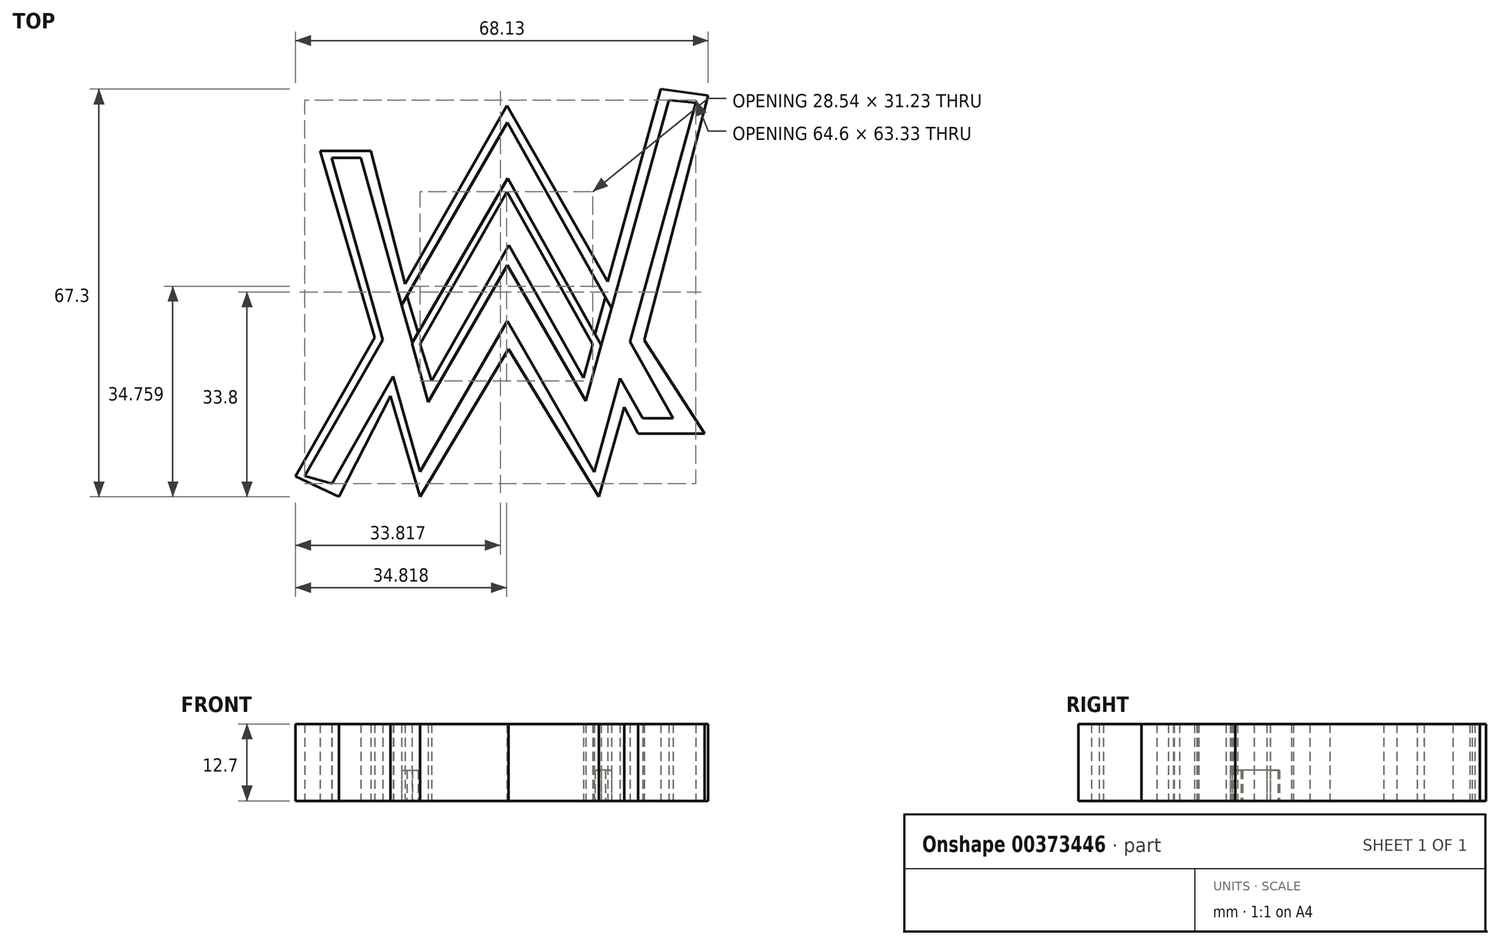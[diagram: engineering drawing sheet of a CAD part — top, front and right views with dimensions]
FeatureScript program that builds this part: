
annotation { "Feature Type Name" : "Feature", "Feature Type Description" : "" }
export const myFeature = defineFeature(function(context is Context, id is Id, definition is map)
    precondition{}
    {
        {
            var Q0;
            Q0=qCreatedBy(makeId("Top.planeOp"),FACE);
            var sketch = newSketch(context, id + "F0", { "sketchPlane" : qUnion([Q0])});
            skLineSegment(sketch, "E0", {"start": v(-32.07, -30.83) * mm, "end": v(-19.22, -8.32) * mm});
            skLineSegment(sketch, "E1", {"start": v(-19.22, -8.32) * mm, "end": v(-27.67, 21.68) * mm});
            skLineSegment(sketch, "E2", {"start": v(-27.67, 21.68) * mm, "end": v(-22.79, 21.68) * mm});
            skLineSegment(sketch, "E3", {"start": v(-22.79, 21.68) * mm, "end": v(-16.07, -2.6) * mm});
            skLineSegment(sketch, "E4", {"start": v(-16.07, -2.6) * mm, "end": v(1.36, 27.56) * mm});
            skLineSegment(sketch, "E5", {"start": v(1.36, 27.56) * mm, "end": v(18.6, -3.14) * mm});
            skLineSegment(sketch, "E6", {"start": v(18.6, -3.14) * mm, "end": v(28.06, 31.21) * mm});
            skLineSegment(sketch, "E7", {"start": v(28.06, 31.21) * mm, "end": v(32.52, 30.76) * mm});
            skLineSegment(sketch, "E8", {"start": v(32.52, 30.76) * mm, "end": v(21.67, -8.63) * mm});
            skLineSegment(sketch, "E9", {"start": v(21.67, -8.63) * mm, "end": v(28.75, -21.3) * mm});
            skLineSegment(sketch, "E10", {"start": v(28.75, -21.3) * mm, "end": v(23.7, -21.3) * mm});
            skLineSegment(sketch, "E11", {"start": v(23.7, -21.3) * mm, "end": v(20, -14.7) * mm});
            skLineSegment(sketch, "E12", {"start": v(20, -14.7) * mm, "end": v(15.7, -30.17) * mm});
            skLineSegment(sketch, "E13", {"start": v(15.7, -30.17) * mm, "end": v(1.36, -5.25) * mm});
            skLineSegment(sketch, "E14", {"start": v(1.36, -5.25) * mm, "end": v(-13.04, -30.13) * mm});
            skLineSegment(sketch, "E15", {"start": v(-13.04, -30.13) * mm, "end": v(-17.44, -14.62) * mm});
            skLineSegment(sketch, "E16", {"start": v(-17.44, -14.62) * mm, "end": v(-17.5, -14.4) * mm});
            skLineSegment(sketch, "E17", {"start": v(-17.5, -14.4) * mm, "end": v(-27.56, -32.11) * mm});
            skLineSegment(sketch, "E18", {"start": v(-27.56, -32.11) * mm, "end": v(-32.07, -30.83) * mm});
            skLineSegment(sketch, "E19", {"start": v(1.43, 18.3) * mm, "end": v(16.89, -9.22) * mm});
            skLineSegment(sketch, "E20", {"start": v(16.89, -9.22) * mm, "end": v(14.34, -18.46) * mm});
            skLineSegment(sketch, "E21", {"start": v(14.34, -18.46) * mm, "end": v(1.37, 3.98) * mm});
            skLineSegment(sketch, "E22", {"start": v(1.37, 3.98) * mm, "end": v(-11.69, -18.6) * mm});
            skLineSegment(sketch, "E23", {"start": v(-11.69, -18.6) * mm, "end": v(-14.35, -8.89) * mm});
            skLineSegment(sketch, "E24", {"start": v(-14.35, -8.89) * mm, "end": v(1.43, 18.3) * mm});
            skLineSegment(sketch, "E25", {"start": v(-33.59, -30.85) * mm, "end": v(-20.52, -7.97) * mm});
            skLineSegment(sketch, "E26", {"start": v(-20.52, -7.97) * mm, "end": v(-29.53, 22.83) * mm});
            skLineSegment(sketch, "E27", {"start": v(-29.53, 22.83) * mm, "end": v(-21.16, 22.83) * mm});
            skLineSegment(sketch, "E28", {"start": v(-21.16, 22.83) * mm, "end": v(-15.52, 0.88) * mm});
            skLineSegment(sketch, "E29", {"start": v(-15.52, 0.88) * mm, "end": v(1.31, 30.35) * mm});
            skLineSegment(sketch, "E30", {"start": v(1.31, 30.35) * mm, "end": v(17.97, 1.23) * mm});
            skLineSegment(sketch, "E31", {"start": v(17.97, 1.23) * mm, "end": v(26.7, 33.05) * mm});
            skLineSegment(sketch, "E32", {"start": v(26.7, 33.05) * mm, "end": v(34.54, 32) * mm});
            skLineSegment(sketch, "E33", {"start": v(34.54, 32) * mm, "end": v(23.97, -8.38) * mm});
            skLineSegment(sketch, "E34", {"start": v(23.97, -8.38) * mm, "end": v(33.97, -23.84) * mm});
            skLineSegment(sketch, "E35", {"start": v(33.97, -23.84) * mm, "end": v(22.95, -23.84) * mm});
            skLineSegment(sketch, "E36", {"start": v(22.95, -23.84) * mm, "end": v(20.71, -19.42) * mm});
            skLineSegment(sketch, "E37", {"start": v(20.71, -19.42) * mm, "end": v(16.51, -34.25) * mm});
            skLineSegment(sketch, "E38", {"start": v(16.51, -34.25) * mm, "end": v(1.55, -9.9) * mm});
            skLineSegment(sketch, "E39", {"start": v(1.55, -9.9) * mm, "end": v(-13.04, -34.25) * mm});
            skLineSegment(sketch, "E40", {"start": v(-13.04, -34.25) * mm, "end": v(-17.9, -17.6) * mm});
            skLineSegment(sketch, "E41", {"start": v(-17.9, -17.6) * mm, "end": v(-26.44, -34.25) * mm});
            skLineSegment(sketch, "E42", {"start": v(-26.44, -34.25) * mm, "end": v(-33.59, -30.85) * mm});
            skLineSegment(sketch, "E43", {"start": v(-13.04, -9.05) * mm, "end": v(1.34, 16.12) * mm});
            skLineSegment(sketch, "E44", {"start": v(1.34, 16.12) * mm, "end": v(15.5, -9.1) * mm});
            skLineSegment(sketch, "E45", {"start": v(15.5, -9.1) * mm, "end": v(13.92, -14.64) * mm});
            skLineSegment(sketch, "E46", {"start": v(13.92, -14.64) * mm, "end": v(1.62, 7.27) * mm});
            skLineSegment(sketch, "E47", {"start": v(1.62, 7.27) * mm, "end": v(-11.16, -15.1) * mm});
            skLineSegment(sketch, "E48", {"start": v(-13.04, -9.05) * mm, "end": v(-11.16, -15.1) * mm});
            skLineSegment(sketch, "E49", {"start": v(-16.07, -2.6) * mm, "end": v(-14.32, -8.89) * mm});
            skLineSegment(sketch, "E50", {"start": v(-15.19, -1.08) * mm, "end": v(-13.35, -7.16) * mm});
            skLineSegment(sketch, "E51", {"start": v(18.6, -3.14) * mm, "end": v(16.89, -9.22) * mm});
            skLineSegment(sketch, "E52", {"start": v(17.56, -1.31) * mm, "end": v(15.86, -7.4) * mm});
            skSolve(sketch);
        }
        {
            var Q0;
            Q0 = qSketchRegion(id + "F0", true);
            var Q1;
            Q1=makeQuery(id+"F0.imprint","IMPRINT",FACE,{"disambiguationData":[TD([[makeQuery(id+"F0.imprint","IMPRINT",EDGE,{"derivedFrom":sQuery(id+"F0.wireOp",EDGE,"E19")}),-1.0]])]});
            extrude(context, id + "F1", {"entities" : qUnion([Q0, Q1]), "depth" : 12.7 * mm});
        }
        {
            var Q0;
            {var subQ3=sQuery(id+"F0.wireOp",EDGE,"E50");Q0=makeQuery(id+"F0.imprint","IMPRINT",FACE,{"disambiguationData":[TD([[makeQuery(id+"F0.imprint","IMPRINT",EDGE,{"derivedFrom":subQ3}),-1.0]])]});}
            var Q1;
            {var subQ0=sQuery(id+"F0.wireOp",EDGE,"E51");Q1=makeQuery(id+"F0.imprint","IMPRINT",FACE,{"disambiguationData":[TD([[makeQuery(id+"F0.imprint","IMPRINT",EDGE,{"derivedFrom":subQ0}),-1.0]])]});}
            extrude(context, id + "F2", {"entities" : qUnion([Q0, Q1]), "depth" : 5.08 * mm});
        }
    });
